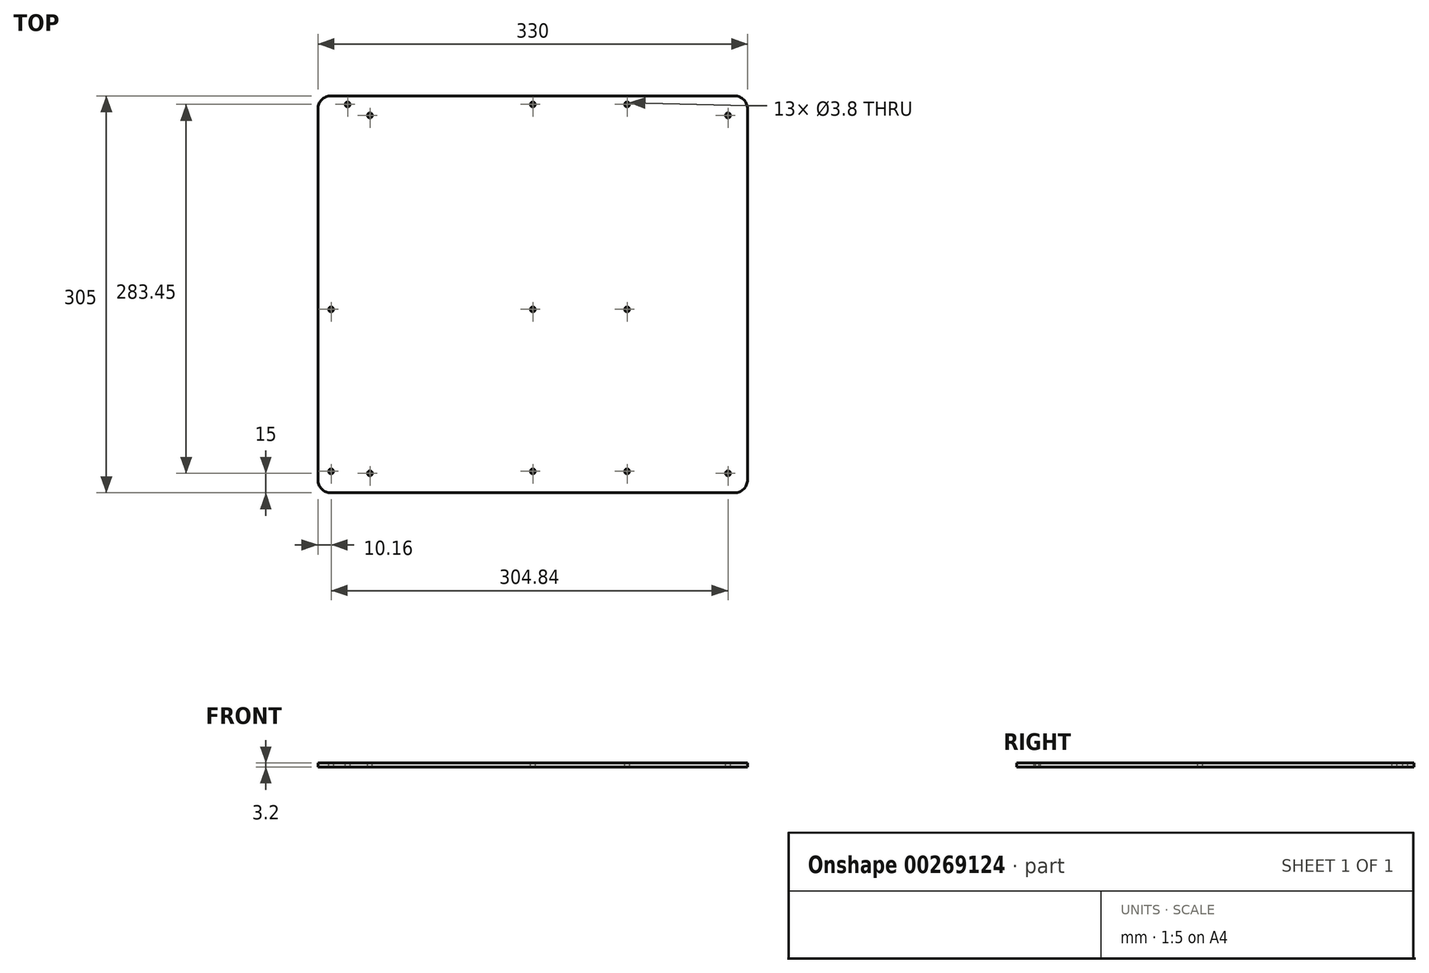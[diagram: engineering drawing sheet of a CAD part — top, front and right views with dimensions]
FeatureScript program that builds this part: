
annotation { "Feature Type Name" : "Feature", "Feature Type Description" : "" }
export const myFeature = defineFeature(function(context is Context, id is Id, definition is map)
    precondition{}
    {
        {
            var Q0;
            Q0=qCreatedBy(makeId("Top.planeOp"),FACE);
            var sketch = newSketch(context, id + "F0", { "sketchPlane" : qUnion([Q0])});
            skLineSegment(sketch, "E0.bottom", {"start": v(155, 147.5) * mm, "end": v(-155, 147.5) * mm});
            skLineSegment(sketch, "E0.top", {"start": v(155, -157.5) * mm, "end": v(-155, -157.5) * mm});
            skLineSegment(sketch, "E0.left", {"start": v(165, 137.5) * mm, "end": v(165, -147.5) * mm});
            skLineSegment(sketch, "E0.right", {"start": v(-165, 137.5) * mm, "end": v(-165, -147.5) * mm});
            skPoint(sketch, "E1.visualSharp", {"position": v(-165, 147.5) * mm});
            skArc(sketch, "E1.filletArc", {"start": v(-155, 147.5) * mm, "mid": v(-162.07, 144.57) * mm, "end": v(-165, 137.5) * mm});
            skPoint(sketch, "E2.visualSharp", {"position": v(165, 147.5) * mm});
            skArc(sketch, "E2.filletArc", {"start": v(165, 137.5) * mm, "mid": v(162.07, 144.57) * mm, "end": v(155, 147.5) * mm});
            skPoint(sketch, "E3.visualSharp", {"position": v(165, -157.5) * mm});
            skArc(sketch, "E3.filletArc", {"start": v(155, -157.5) * mm, "mid": v(162.07, -154.57) * mm, "end": v(165, -147.5) * mm});
            skPoint(sketch, "E4.visualSharp", {"position": v(-165, -157.5) * mm});
            skArc(sketch, "E4.filletArc", {"start": v(-165, -147.5) * mm, "mid": v(-162.07, -154.57) * mm, "end": v(-155, -157.5) * mm});
            skSolve(sketch);
        }
        {
            var Q0;
            Q0=makeQuery(id+"F0.imprint","IMPRINT",FACE,{"disambiguationData":[TD([[makeQuery(id+"F0.imprint","IMPRINT",EDGE,{"derivedFrom":sQuery(id+"F0.wireOp",EDGE,"E0.bottom")}),1.0]])]});
            extrude(context, id + "F1", {"entities" : qUnion([Q0]), "depth" : 3.2 * mm});
        }
        {
            var Q0;
            Q0=makeQuery(id+"F1.opExtrude","CAP_FACE",FACE,{"disambiguationData":[OSD([sQuery(id+"F0.wireOp",EDGE,"E0.bottom"),sQuery(id+"F0.wireOp",EDGE,"E0.top"),sQuery(id+"F0.wireOp",EDGE,"E0.left"),sQuery(id+"F0.wireOp",EDGE,"E0.right")])],"isStart":false});
            var sketch = newSketch(context, id + "F2", { "sketchPlane" : qUnion([Q0])});
            skPoint(sketch, "E5", {"position": v(-125, 132.5) * mm});
            skPoint(sketch, "E6", {"position": v(150, 132.5) * mm});
            skPoint(sketch, "E7", {"position": v(150, -142.5) * mm});
            skPoint(sketch, "E8", {"position": v(-125, -142.5) * mm});
            skSolve(sketch);
        }
        {
            var Q0;
            Q0=sQuery(id+"F2.wireOp",VERTEX,"E5");
            var Q1;
            Q1=sQuery(id+"F2.wireOp",VERTEX,"E6");
            var Q2;
            Q2=sQuery(id+"F2.wireOp",VERTEX,"E7");
            var Q3;
            Q3=sQuery(id+"F2.wireOp",VERTEX,"E8");
            var Q4;
            Q4=makeQuery(id+"F1.opExtrude","SWEPT_BODY",BODY,{"disambiguationData":[OSD([sQuery(id+"F0.wireOp",EDGE,"E0.bottom"),sQuery(id+"F0.wireOp",EDGE,"E0.top"),sQuery(id+"F0.wireOp",EDGE,"E0.left"),sQuery(id+"F0.wireOp",EDGE,"E0.right")])]});
            hole(context, id + "F3", {"style" : HoleStyle.SIMPLE, "endStyle" : HoleEndStyle.THROUGH, "standardTappedOrClearance" : lookupTablePath({ "standard" : "ANSI", "fit" : "Normal (ASME)", "size" : "#6", "type" : "Clearance" }), "standardBlindInLast" : lookupTablePath({ "fit" : "Free", "standard" : "ANSI", "size" : "#6", "type" : "Clearance" }), "holeDiameter" : 3.8 * mm, "tappedDepth" : 12 * mm, "tapClearance" : 3, "locations" : qUnion([Q0, Q1, Q2, Q3]), "scope" : qUnion([Q4])});
        }
        {
            var Q0;
            Q0=makeQuery(id+"F1.opExtrude","CAP_FACE",FACE,{"disambiguationData":[OSD([sQuery(id+"F0.wireOp",EDGE,"E0.bottom"),sQuery(id+"F0.wireOp",EDGE,"E0.top"),sQuery(id+"F0.wireOp",EDGE,"E0.left"),sQuery(id+"F0.wireOp",EDGE,"E0.right")])],"isStart":false});
            var sketch = newSketch(context, id + "F4", { "sketchPlane" : qUnion([Q0])});
            skPoint(sketch, "E9", {"position": v(-142.14, 140.95) * mm});
            skPoint(sketch, "E10", {"position": v(0.1, 140.95) * mm});
            skPoint(sketch, "E11", {"position": v(72.5, 140.95) * mm});
            skPoint(sketch, "E12", {"position": v(-154.84, -16.53) * mm});
            skPoint(sketch, "E13", {"position": v(0.1, -16.53) * mm});
            skPoint(sketch, "E14", {"position": v(72.5, -16.53) * mm});
            skPoint(sketch, "E15", {"position": v(72.5, -140.99) * mm});
            skPoint(sketch, "E16", {"position": v(0.1, -140.99) * mm});
            skPoint(sketch, "E17", {"position": v(-154.84, -140.99) * mm});
            skSolve(sketch);
        }
        {
            var Q0;
            Q0=sQuery(id+"F4.wireOp",VERTEX,"E9");
            var Q1;
            Q1=sQuery(id+"F4.wireOp",VERTEX,"E10");
            var Q2;
            Q2=sQuery(id+"F4.wireOp",VERTEX,"E11");
            var Q3;
            Q3=sQuery(id+"F4.wireOp",VERTEX,"E12");
            var Q4;
            Q4=sQuery(id+"F4.wireOp",VERTEX,"E13");
            var Q5;
            Q5=sQuery(id+"F4.wireOp",VERTEX,"E14");
            var Q6;
            Q6=sQuery(id+"F4.wireOp",VERTEX,"E15");
            var Q7;
            Q7=sQuery(id+"F4.wireOp",VERTEX,"E16");
            var Q8;
            Q8=sQuery(id+"F4.wireOp",VERTEX,"E17");
            var Q9;
            Q9=makeQuery(id+"F1.opExtrude","SWEPT_BODY",BODY,{"disambiguationData":[OSD([sQuery(id+"F0.wireOp",EDGE,"E0.bottom"),sQuery(id+"F0.wireOp",EDGE,"E0.top"),sQuery(id+"F0.wireOp",EDGE,"E0.left"),sQuery(id+"F0.wireOp",EDGE,"E0.right")])]});
            hole(context, id + "F5", {"style" : HoleStyle.SIMPLE, "endStyle" : HoleEndStyle.THROUGH, "standardTappedOrClearance" : lookupTablePath({ "standard" : "ANSI", "fit" : "Normal (ASME)", "size" : "#6", "type" : "Clearance" }), "standardBlindInLast" : lookupTablePath({ "fit" : "Free", "standard" : "ANSI", "size" : "#6", "type" : "Clearance" }), "holeDiameter" : 3.8 * mm, "tappedDepth" : 12 * mm, "tapClearance" : 3, "locations" : qUnion([Q0, Q1, Q2, Q3, Q4, Q5, Q6, Q7, Q8]), "scope" : qUnion([Q9])});
        }
    });
